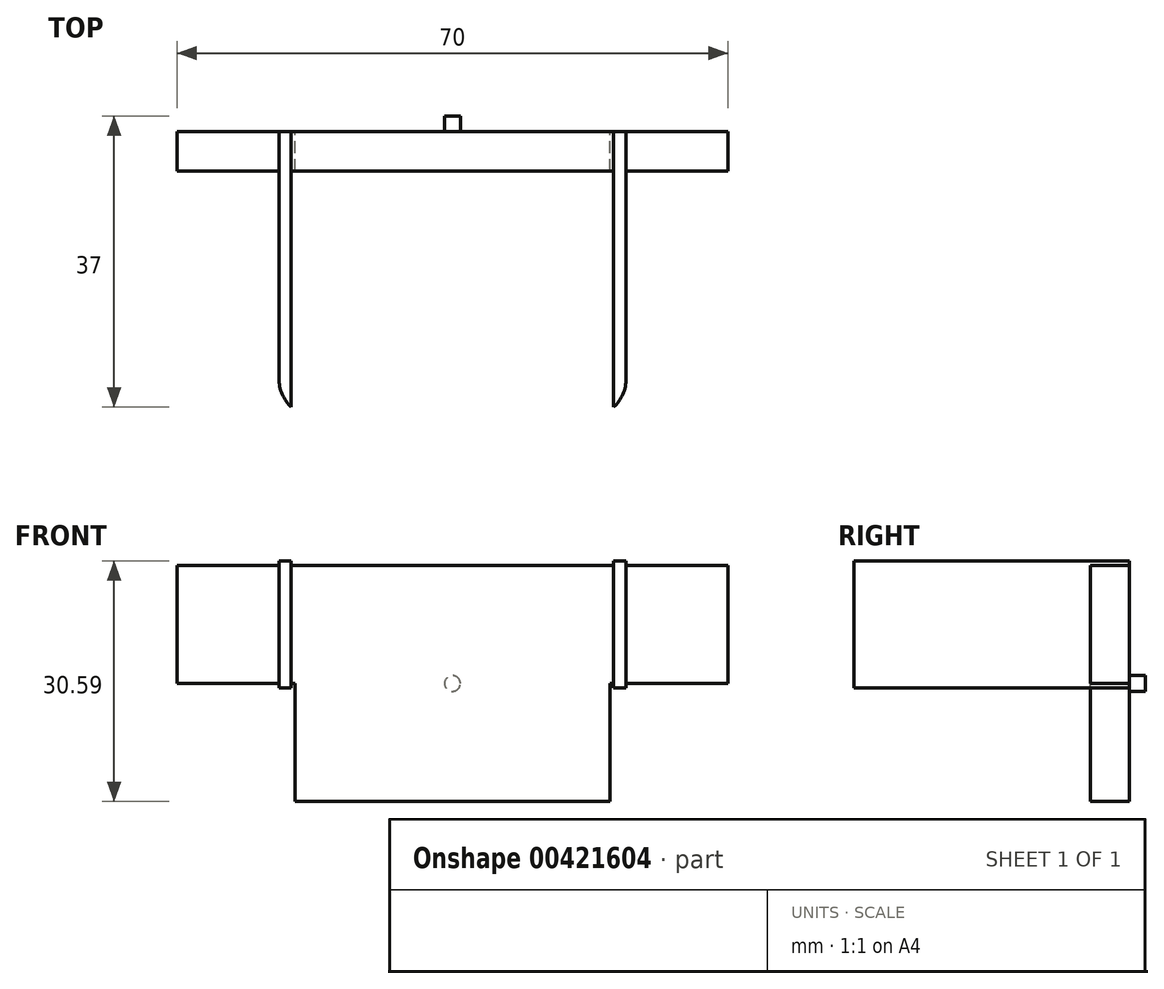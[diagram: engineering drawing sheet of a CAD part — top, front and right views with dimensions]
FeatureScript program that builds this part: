
annotation { "Feature Type Name" : "Feature", "Feature Type Description" : "" }
export const myFeature = defineFeature(function(context is Context, id is Id, definition is map)
    precondition{}
    {
        {
            var Q0;
            Q0=qCreatedBy(makeId("Front.planeOp"),FACE);
            var sketch = newSketch(context, id + "F0", { "sketchPlane" : qUnion([Q0])});
            skLineSegment(sketch, "E0.bottom", {"start": v(35, 15) * mm, "end": v(-35, 15) * mm});
            skPoint(sketch, "E0.middle", {"position": v(0, 0) * mm});
            skLineSegment(sketch, "E1.top", {"start": v(20, -15) * mm, "end": v(-20, -15) * mm});
            skLineSegment(sketch, "E2", {"start": v(-35, 0) * mm, "end": v(-20, 0) * mm});
            skLineSegment(sketch, "E3", {"start": v(20, 0) * mm, "end": v(35, 0) * mm});
            skLineSegment(sketch, "E4", {"start": v(-35, 0) * mm, "end": v(-35, 15) * mm});
            skLineSegment(sketch, "E5", {"start": v(35, 0) * mm, "end": v(35, 15) * mm});
            skLineSegment(sketch, "E6", {"start": v(-20, -15) * mm, "end": v(-20, 0) * mm});
            skLineSegment(sketch, "E7", {"start": v(20, -15) * mm, "end": v(20, 0) * mm});
            skLineSegment(sketch, "E8.bottom", {"start": v(22.05, -0.58) * mm, "end": v(20.48, -0.58) * mm});
            skLineSegment(sketch, "E8.top", {"start": v(22.05, 15.59) * mm, "end": v(20.48, 15.59) * mm});
            skLineSegment(sketch, "E8.left", {"start": v(22.05, -0.58) * mm, "end": v(22.05, 15.59) * mm});
            skLineSegment(sketch, "E8.right", {"start": v(20.48, -0.58) * mm, "end": v(20.48, 15.59) * mm});
            skLineSegment(sketch, "E9.MirrorCS", {"start": v(-20.48, -0.58) * mm, "end": v(-20.48, 15.59) * mm});
            skLineSegment(sketch, "E10.MirrorCS", {"start": v(-22.05, 15.59) * mm, "end": v(-20.48, 15.59) * mm});
            skLineSegment(sketch, "E11.MirrorCS", {"start": v(-22.05, -0.58) * mm, "end": v(-22.05, 15.59) * mm});
            skLineSegment(sketch, "E12.MirrorCS", {"start": v(-22.05, -0.58) * mm, "end": v(-20.48, -0.58) * mm});
            skCircle(sketch, "E13", {"center": v(0, 0) * mm, "radius": 1 * mm});
            skSolve(sketch);
        }
        {
            var Q0;
            {var subQ0=sQuery(id+"F0.wireOp",EDGE,"pc3wgerc-33Hj-Agl0-1XD8-YdpxQaCQ7Cax");Q0=makeQuery(id+"F0.imprint","IMPRINT",FACE,{"disambiguationData":[TD([[makeQuery(id+"F0.imprint","IMPRINT",EDGE,{"derivedFrom":subQ0}),1.0]])]});}
            var Q1;
            Q1=makeQuery(id+"F0.imprint","IMPRINT",FACE,{"disambiguationData":[TD([[makeQuery(id+"F0.imprint","IMPRINT",EDGE,{"derivedFrom":sQuery(id+"F0.wireOp",EDGE,"Rg9MMUDl-VrJG-9IUq-TfrW-nv2eMUZ4gA35")}),-1.0]])]});
            var Q2;
            {var subQ0=sQuery(id+"F0.wireOp",EDGE,"q7pJYDEW-rlHR-lqUo-Ut0C-9f3HIwKl5fn7.right");var subQ1=sQuery(id+"F0.wireOp",EDGE,"hibQ91mv-OWds-nG4l-SPJ5-Oq8z9B343iiP.bottom");var subQ2=makeQuery(id+"F0.imprint","INTERSECT",VERTEX,{"derivedFrom":[subQ1,subQ0]});Q2=makeQuery(id+"F0.imprint","IMPRINT",FACE,{"disambiguationData":[TD([[makeQuery(id+"F0.imprint","IMPRINT",EDGE,{"disambiguationData":[TD([[subQ2,-1.0]])],"derivedFrom":subQ1}),1.0]])]});}
            var Q3;
            {var subQ0=sQuery(id+"F0.wireOp",EDGE,"Q5jxO8zj-ssWH-Y7JB-M17k-WKEKGxbXXx6T");Q3=makeQuery(id+"F0.imprint","IMPRINT",FACE,{"disambiguationData":[TD([[makeQuery(id+"F0.imprint","IMPRINT",EDGE,{"derivedFrom":subQ0}),-1.0]])]});}
            var Q4;
            {var subQ0=sQuery(id+"F0.wireOp",EDGE,"8c918a50-f1c1-467d-8542-b7941378079b0.MirrorCS");var subQ1=sQuery(id+"F0.wireOp",EDGE,"hibQ91mv-OWds-nG4l-SPJ5-Oq8z9B343iiP.bottom");var subQ2=makeQuery(id+"F0.imprint","INTERSECT",VERTEX,{"derivedFrom":[subQ1,subQ0]});Q4=makeQuery(id+"F0.imprint","IMPRINT",FACE,{"disambiguationData":[TD([[makeQuery(id+"F0.imprint","IMPRINT",EDGE,{"disambiguationData":[TD([[subQ2,-1.0]])],"derivedFrom":subQ1}),1.0]])]});}
            var Q5;
            Q5=makeQuery(id+"F0.imprint","IMPRINT",FACE,{"disambiguationData":[TD([[makeQuery(id+"F0.imprint","IMPRINT",EDGE,{"derivedFrom":sQuery(id+"F0.wireOp",EDGE,"Rg9MMUDl-VrJG-9IUq-TfrW-nv2eMUZ4gA35")}),1.0]])]});
            var Q6;
            {var subQ0=sQuery(id+"F0.wireOp",EDGE,"E4");Q6=makeQuery(id+"F0.imprint","IMPRINT",FACE,{"disambiguationData":[TD([[makeQuery(id+"F0.imprint","IMPRINT",EDGE,{"derivedFrom":subQ0}),-1.0]])]});}
            var Q7;
            Q7=makeQuery(id+"F0.imprint","IMPRINT",FACE,{"disambiguationData":[TD([[makeQuery(id+"F0.imprint","IMPRINT",EDGE,{"derivedFrom":sQuery(id+"F0.wireOp",EDGE,"E1.top")}),-1.0]])]});
            var Q8;
            {var subQ0=sQuery(id+"F0.wireOp",EDGE,"E9.MirrorCS");var subQ1=sQuery(id+"F0.wireOp",EDGE,"E0.bottom");var subQ2=makeQuery(id+"F0.imprint","INTERSECT",VERTEX,{"derivedFrom":[subQ1,subQ0]});Q8=makeQuery(id+"F0.imprint","IMPRINT",FACE,{"disambiguationData":[TD([[makeQuery(id+"F0.imprint","IMPRINT",EDGE,{"disambiguationData":[TD([[subQ2,-1.0]])],"derivedFrom":subQ1}),1.0]])]});}
            var Q9;
            {var subQ0=sQuery(id+"F0.wireOp",EDGE,"E8.left");var subQ1=sQuery(id+"F0.wireOp",EDGE,"E0.bottom");var subQ2=makeQuery(id+"F0.imprint","INTERSECT",VERTEX,{"derivedFrom":[subQ1,subQ0]});Q9=makeQuery(id+"F0.imprint","IMPRINT",FACE,{"disambiguationData":[TD([[makeQuery(id+"F0.imprint","IMPRINT",EDGE,{"disambiguationData":[TD([[subQ2,-1.0]])],"derivedFrom":subQ1}),1.0]])]});}
            var Q10;
            {var subQ0=sQuery(id+"F0.wireOp",EDGE,"E5");Q10=makeQuery(id+"F0.imprint","IMPRINT",FACE,{"disambiguationData":[TD([[makeQuery(id+"F0.imprint","IMPRINT",EDGE,{"derivedFrom":subQ0}),1.0]])]});}
            var Q11;
            Q11=makeQuery(id+"F0.imprint","IMPRINT",FACE,{"disambiguationData":[TD([[makeQuery(id+"F0.imprint","IMPRINT",EDGE,{"derivedFrom":sQuery(id+"F0.wireOp",EDGE,"E13")}),1.0]])]});
            extrude(context, id + "F1", {"entities" : qUnion([Q0, Q1, Q2, Q3, Q4, Q5, Q6, Q7, Q8, Q9, Q10, Q11]), "depth" : 5 * mm});
        }
        {
            var Q0;
            Q0=makeQuery(id+"F0.imprint","IMPRINT",FACE,{"disambiguationData":[TD([[makeQuery(id+"F0.imprint","IMPRINT",EDGE,{"derivedFrom":sQuery(id+"F0.wireOp",EDGE,"E13")}),1.0]])]});
            extrude(context, id + "F2", {"entities" : qUnion([Q0]), "operationType" : NewBodyOperationType.ADD, "oppositeDirection" : true, "depth" : 2 * mm});
        }
        {
            var Q0;
            {var subQ0=sQuery(id+"F0.wireOp",EDGE,"E9.MirrorCS");var subQ1=sQuery(id+"F0.wireOp",EDGE,"E0.bottom");var subQ2=makeQuery(id+"F0.imprint","INTERSECT",VERTEX,{"derivedFrom":[subQ1,subQ0]});Q0=makeQuery(id+"F0.imprint","IMPRINT",FACE,{"disambiguationData":[TD([[makeQuery(id+"F0.imprint","IMPRINT",EDGE,{"disambiguationData":[TD([[subQ2,-1.0]])],"derivedFrom":subQ1}),1.0]])]});}
            var Q1;
            {var subQ5=sQuery(id+"F0.wireOp",EDGE,"E12.MirrorCS");Q1=makeQuery(id+"F0.imprint","IMPRINT",FACE,{"disambiguationData":[TD([[makeQuery(id+"F0.imprint","IMPRINT",EDGE,{"derivedFrom":subQ5}),1.0]])]});}
            var Q2;
            {var subQ5=sQuery(id+"F0.wireOp",EDGE,"E10.MirrorCS");Q2=makeQuery(id+"F0.imprint","IMPRINT",FACE,{"disambiguationData":[TD([[makeQuery(id+"F0.imprint","IMPRINT",EDGE,{"derivedFrom":subQ5}),-1.0]])]});}
            var Q3;
            {var subQ5=sQuery(id+"F0.wireOp",EDGE,"E8.top");Q3=makeQuery(id+"F0.imprint","IMPRINT",FACE,{"disambiguationData":[TD([[makeQuery(id+"F0.imprint","IMPRINT",EDGE,{"derivedFrom":subQ5}),1.0]])]});}
            var Q4;
            {var subQ0=sQuery(id+"F0.wireOp",EDGE,"E8.left");var subQ1=sQuery(id+"F0.wireOp",EDGE,"E0.bottom");var subQ2=makeQuery(id+"F0.imprint","INTERSECT",VERTEX,{"derivedFrom":[subQ1,subQ0]});Q4=makeQuery(id+"F0.imprint","IMPRINT",FACE,{"disambiguationData":[TD([[makeQuery(id+"F0.imprint","IMPRINT",EDGE,{"disambiguationData":[TD([[subQ2,-1.0]])],"derivedFrom":subQ1}),1.0]])]});}
            var Q5;
            {var subQ5=sQuery(id+"F0.wireOp",EDGE,"E8.bottom");Q5=makeQuery(id+"F0.imprint","IMPRINT",FACE,{"disambiguationData":[TD([[makeQuery(id+"F0.imprint","IMPRINT",EDGE,{"derivedFrom":subQ5}),-1.0]])]});}
            extrude(context, id + "F3", {"entities" : qUnion([Q0, Q1, Q2, Q3, Q4, Q5]), "operationType" : NewBodyOperationType.ADD, "depth" : 35 * mm});
        }
        {
            var Q0;
            Q0=makeQuery(id+"F3.opExtrude","CAP_EDGE",EDGE,{"disambiguationData":[OSD([sQuery(id+"F0.wireOp",EDGE,"E11.MirrorCS")])],"isStart":false});
            var Q1;
            Q1=makeQuery(id+"F3.opExtrude","CAP_EDGE",EDGE,{"disambiguationData":[OSD([sQuery(id+"F0.wireOp",EDGE,"E8.left")])],"isStart":false});
            fillet(context, id + "F4", {"entities" : qUnion([Q0, Q1]), "radius" : 5 * mm, "tangentPropagation" : true, "allowEdgeOverflow" : false});
        }
    });
